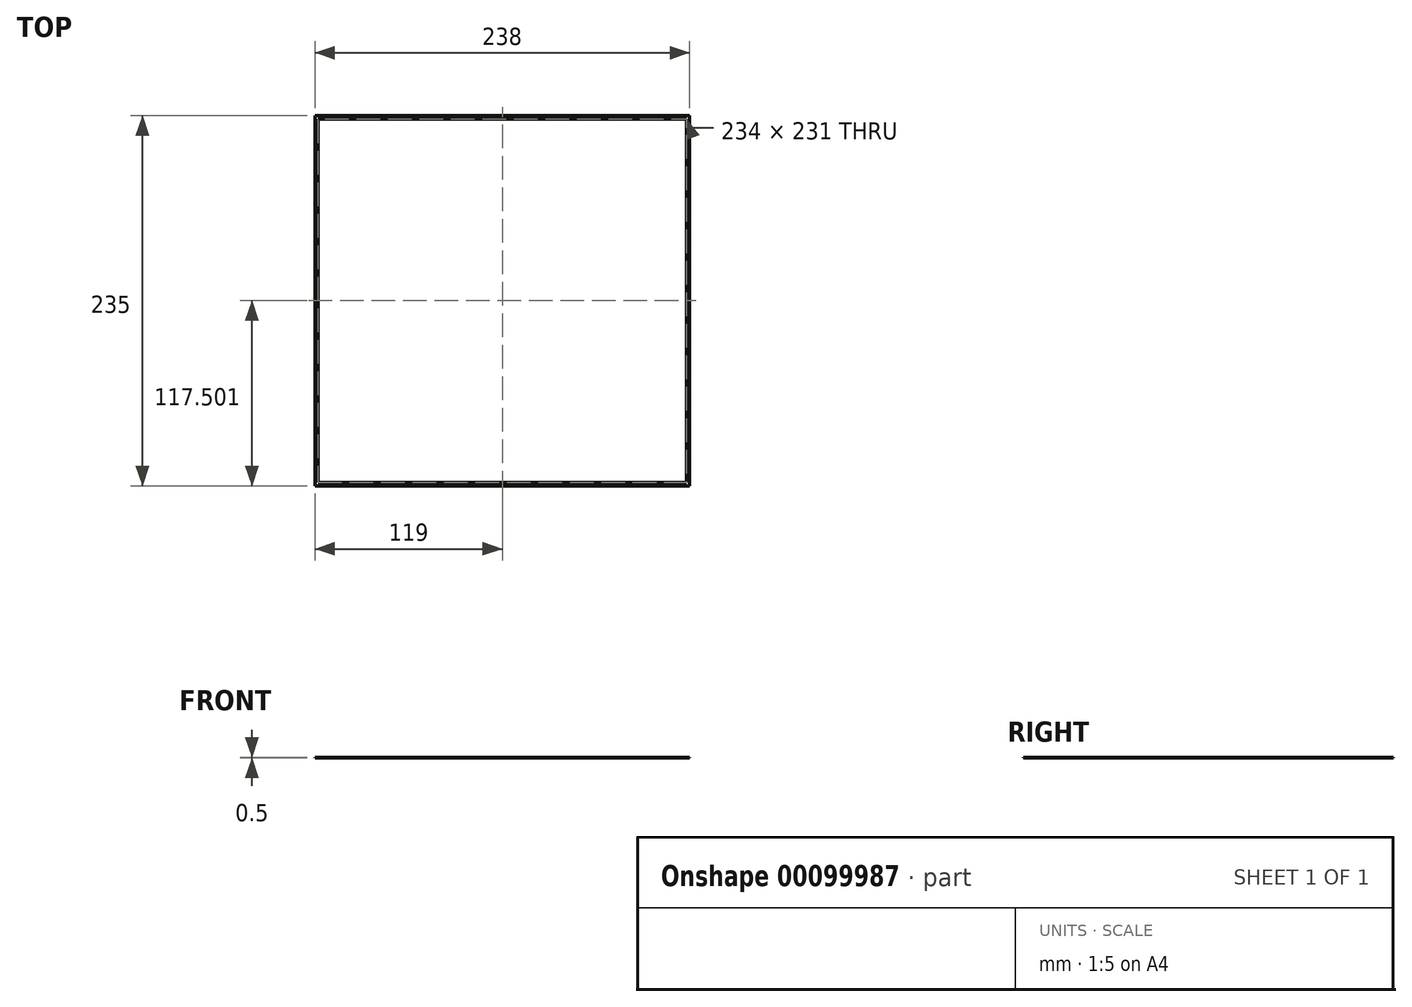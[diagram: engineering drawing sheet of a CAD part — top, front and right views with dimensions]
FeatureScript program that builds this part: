
annotation { "Feature Type Name" : "Feature", "Feature Type Description" : "" }
export const myFeature = defineFeature(function(context is Context, id is Id, definition is map)
    precondition{}
    {
        {
            var Q0;
            Q0=qCreatedBy(makeId("Top.planeOp"),FACE);
            var sketch = newSketch(context, id + "F0", { "sketchPlane" : qUnion([Q0])});
            skLineSegment(sketch, "E0.bottom", {"start": v(-175.6, 169.35) * mm, "end": v(62.4, 169.35) * mm});
            skLineSegment(sketch, "E0.top", {"start": v(-175.6, -65.65) * mm, "end": v(62.4, -65.65) * mm});
            skLineSegment(sketch, "E0.left", {"start": v(-175.6, 169.35) * mm, "end": v(-175.6, -65.65) * mm});
            skLineSegment(sketch, "E0.right", {"start": v(62.4, 169.35) * mm, "end": v(62.4, -65.65) * mm});
            skLineSegment(sketch, "E1.0", {"start": v(-173.6, 167.35) * mm, "end": v(60.4, 167.35) * mm});
            skLineSegment(sketch, "E1.1", {"start": v(-173.6, 167.35) * mm, "end": v(-173.6, -63.65) * mm});
            skLineSegment(sketch, "E1.2", {"start": v(-173.6, -63.65) * mm, "end": v(60.4, -63.65) * mm});
            skLineSegment(sketch, "E1.3", {"start": v(60.4, 167.35) * mm, "end": v(60.4, -63.65) * mm});
            skSolve(sketch);
        }
        {
            var Q0;
            Q0=makeQuery(id+"F0.imprint","IMPRINT",FACE,{"disambiguationData":[TD([[makeQuery(id+"F0.imprint","IMPRINT",EDGE,{"derivedFrom":sQuery(id+"F0.wireOp",EDGE,"E0.bottom")}),-1.0]])]});
            extrude(context, id + "F1", {"entities" : qUnion([Q0]), "depth" : 0.5 * mm});
        }
    });
